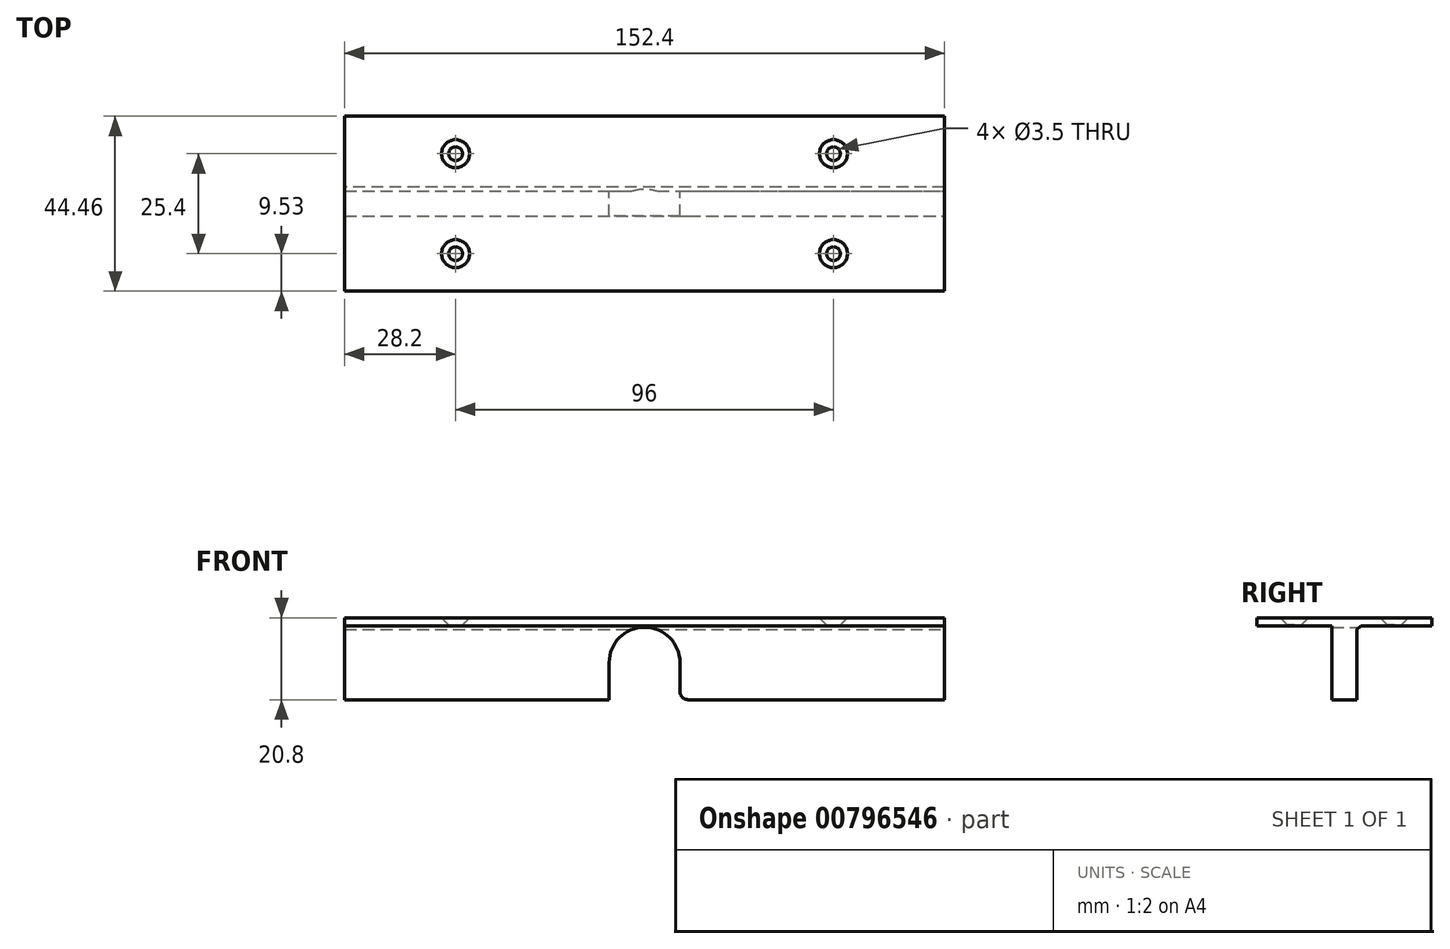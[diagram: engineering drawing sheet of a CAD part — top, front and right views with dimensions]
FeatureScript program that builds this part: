
annotation { "Feature Type Name" : "Feature", "Feature Type Description" : "" }
export const myFeature = defineFeature(function(context is Context, id is Id, definition is map)
    precondition{}
    {
        {
            var Q0;
            Q0=qCreatedBy(makeId("Top.planeOp"),FACE);
            var sketch = newSketch(context, id + "F0", { "sketchPlane" : qUnion([Q0])});
            skLineSegment(sketch, "E0.bottom", {"start": v(76.2, -22.23) * mm, "end": v(-76.2, -22.23) * mm});
            skLineSegment(sketch, "E0.top", {"start": v(76.2, 22.22) * mm, "end": v(-76.2, 22.22) * mm});
            skLineSegment(sketch, "E0.left", {"start": v(76.2, -22.23) * mm, "end": v(76.2, 22.22) * mm});
            skLineSegment(sketch, "E0.right", {"start": v(-76.2, -22.23) * mm, "end": v(-76.2, 22.22) * mm});
            skPoint(sketch, "E0.middle", {"position": v(0, 0) * mm});
            skSolve(sketch);
        }
        {
            var Q0;
            Q0=qSketchRegion(id+"F0",true);
            extrude(context, id + "F1", {"entities" : qUnion([Q0]), "depth" : 2 * mm, "offsetDistance" : 25 * mm});
        }
        {
            var Q0;
            Q0=makeQuery(id+"F1.opExtrude","CAP_FACE",FACE,{"disambiguationData":[OSD([sQuery(id+"F0.wireOp",EDGE,"E0.bottom"),sQuery(id+"F0.wireOp",EDGE,"E0.top"),sQuery(id+"F0.wireOp",EDGE,"E0.left"),sQuery(id+"F0.wireOp",EDGE,"E0.right")])],"isStart":true});
            var sketch = newSketch(context, id + "F2", { "sketchPlane" : qUnion([Q0])});
            skLineSegment(sketch, "E1.bottom", {"start": v(-76.2, -3.18) * mm, "end": v(76.2, -3.18) * mm});
            skLineSegment(sketch, "E1.top", {"start": v(-76.2, 3.17) * mm, "end": v(76.2, 3.17) * mm});
            skLineSegment(sketch, "E1.left", {"start": v(-76.2, -3.18) * mm, "end": v(-76.2, 3.18) * mm});
            skLineSegment(sketch, "E1.right", {"start": v(76.2, -3.18) * mm, "end": v(76.2, 3.18) * mm});
            skPoint(sketch, "E1.middle", {"position": v(0, 0) * mm});
            skSolve(sketch);
        }
        {
            var Q0;
            Q0=makeQuery(id+"F2.imprint","IMPRINT",FACE,{"disambiguationData":[TD([[makeQuery(id+"F2.imprint","IMPRINT",EDGE,{"derivedFrom":sQuery(id+"F2.wireOp",EDGE,"E1.bottom")}),1.0]])]});
            extrude(context, id + "F3", {"entities" : qUnion([Q0]), "operationType" : NewBodyOperationType.ADD, "depth" : 18.8 * mm, "offsetDistance" : 25 * mm});
        }
        {
            var Q0;
            {var subQ0=sQuery(id+"F0.wireOp",EDGE,"E0.right");var subQ1=sQuery(id+"F0.wireOp",EDGE,"E0.left");var subQ2=sQuery(id+"F0.wireOp",EDGE,"E0.top");Q0=makeQuery(id+"F3.boolean.opBoolean","SPLIT",FACE,{"disambiguationData":[TD([makeQuery(id+"F1.opExtrude","SWEPT_FACE",FACE,{"disambiguationData":[OSD([subQ2])]})])],"derivedFrom":makeQuery(id+"F1.opExtrude","CAP_FACE",FACE,{"disambiguationData":[OSD([sQuery(id+"F0.wireOp",EDGE,"E0.bottom"),subQ2,subQ1,subQ0])],"isStart":true})});}
            var sketch = newSketch(context, id + "F4", { "sketchPlane" : qUnion([Q0])});
            skLineSegment(sketch, "E2", {"start": v(76.2, -12.7) * mm, "end": v(-76.2, -12.7) * mm, "construction": true});
            skCircle(sketch, "E3", {"center": v(48, -12.7) * mm, "radius": 1.75 * mm});
            skCircle(sketch, "E4.0.1.0", {"center": v(48, 12.7) * mm, "radius": 1.75 * mm});
            skCircle(sketch, "E4.1.0.0", {"center": v(-48, -12.7) * mm, "radius": 1.75 * mm});
            skCircle(sketch, "E4.1.1.0", {"center": v(-48, 12.7) * mm, "radius": 1.75 * mm});
            skLineSegment(sketch, "E4.direction1", {"start": v(48, -12.7) * mm, "end": v(-48, -12.7) * mm, "construction": true});
            skLineSegment(sketch, "E4.direction2", {"start": v(48, -12.7) * mm, "end": v(48, 12.7) * mm, "construction": true});
            skSolve(sketch);
        }
        {
            var Q0;
            Q0=makeQuery(id+"F4.imprint","IMPRINT",FACE,{"disambiguationData":[TD([[makeQuery(id+"F4.imprint","IMPRINT",EDGE,{"derivedFrom":sQuery(id+"F4.wireOp",EDGE,"E3")}),1.0]])]});
            var Q1;
            Q1=makeQuery(id+"F4.imprint","IMPRINT",FACE,{"disambiguationData":[TD([[makeQuery(id+"F4.imprint","IMPRINT",EDGE,{"derivedFrom":sQuery(id+"F4.wireOp",EDGE,"E4.1.0.0")}),1.0]])]});
            var Q2;
            Q2=makeQuery(id+"F4.imprint","IMPRINT",FACE,{"disambiguationData":[TD([[makeQuery(id+"F4.imprint","IMPRINT",EDGE,{"derivedFrom":sQuery(id+"F4.wireOp",EDGE,"E4.2.0.0")}),1.0]])]});
            var Q3;
            Q3=makeQuery(id+"F4.imprint","IMPRINT",FACE,{"disambiguationData":[TD([[makeQuery(id+"F4.imprint","IMPRINT",EDGE,{"derivedFrom":sQuery(id+"F4.wireOp",EDGE,"E4.3.0.0")}),1.0]])]});
            var Q4;
            Q4=makeQuery(id+"F4.imprint","IMPRINT",FACE,{"disambiguationData":[TD([[makeQuery(id+"F4.imprint","IMPRINT",EDGE,{"derivedFrom":sQuery(id+"F4.wireOp",EDGE,"E4.3.1.0")}),1.0]])]});
            var Q5;
            Q5=makeQuery(id+"F4.imprint","IMPRINT",FACE,{"disambiguationData":[TD([[makeQuery(id+"F4.imprint","IMPRINT",EDGE,{"derivedFrom":sQuery(id+"F4.wireOp",EDGE,"E4.2.1.0")}),1.0]])]});
            var Q6;
            Q6=makeQuery(id+"F4.imprint","IMPRINT",FACE,{"disambiguationData":[TD([[makeQuery(id+"F4.imprint","IMPRINT",EDGE,{"derivedFrom":sQuery(id+"F4.wireOp",EDGE,"E4.1.1.0")}),1.0]])]});
            var Q7;
            Q7=makeQuery(id+"F4.imprint","IMPRINT",FACE,{"disambiguationData":[TD([[makeQuery(id+"F4.imprint","IMPRINT",EDGE,{"derivedFrom":sQuery(id+"F4.wireOp",EDGE,"E4.0.1.0")}),1.0]])]});
            extrude(context, id + "F5", {"entities" : qUnion([Q0, Q1, Q2, Q3, Q4, Q5, Q6, Q7]), "operationType" : NewBodyOperationType.REMOVE, "oppositeDirection" : true, "depth" : 25 * mm, "offsetDistance" : 25 * mm});
        }
        {
            var Q0;
            Q0=makeQuery(id+"F3.opExtrude","SWEPT_FACE",FACE,{"disambiguationData":[OSD([sQuery(id+"F2.wireOp",EDGE,"E1.bottom")])]});
            var sketch = newSketch(context, id + "F6", { "sketchPlane" : qUnion([Q0])});
            skLineSegment(sketch, "E5", {"start": v(-76.2, -9.4) * mm, "end": v(76.2, -9.4) * mm, "construction": true});
            skCircle(sketch, "E6", {"center": v(0, -9.4) * mm, "radius": 9 * mm});
            skCircle(sketch, "E7", {"center": v(0, -9.4) * mm, "radius": 4.76 * mm, "construction": true});
            skPoint(sketch, "E8", {"position": v(9, -9.4) * mm});
            skPoint(sketch, "E9", {"position": v(-9, -9.4) * mm});
            skLineSegment(sketch, "E10", {"start": v(-9, -9.4) * mm, "end": v(-9, -18.8) * mm});
            skLineSegment(sketch, "E11", {"start": v(9, -9.4) * mm, "end": v(9, -18.8) * mm});
            skLineSegment(sketch, "E12", {"start": v(9, -18.8) * mm, "end": v(-9, -18.8) * mm});
            skSolve(sketch);
        }
        {
            var Q0;
            Q0=makeQuery(id+"F6.imprint","IMPRINT",FACE,{"disambiguationData":[TD([[makeQuery(id+"F6.imprint","IMPRINT",EDGE,{"derivedFrom":sQuery(id+"F6.wireOp",EDGE,"E6")}),1.0]])]});
            var Q1;
            {var subQ0=sQuery(id+"F6.wireOp",EDGE,"E10");Q1=makeQuery(id+"F6.imprint","IMPRINT",FACE,{"disambiguationData":[TD([[makeQuery(id+"F6.imprint","IMPRINT",EDGE,{"derivedFrom":subQ0}),1.0]])]});}
            var Q2;
            Q2=sQuery(id+"F6.wireOp",EDGE,"E6");
            extrude(context, id + "F7", {"entities" : qUnion([Q0, Q1]), "operationType" : NewBodyOperationType.REMOVE, "surfaceEntities" : qUnion([Q2]), "endBound" : BoundingType.THROUGH_ALL, "oppositeDirection" : true, "depth" : 25 * mm, "offsetDistance" : 25 * mm});
        }
        {
            var Q0;
            Q0=makeQuery(id+"F5.boolean.opBoolean","INTERSECT",EDGE,{"derivedFrom":[makeQuery(id+"F1.opExtrude","CAP_FACE",FACE,{"disambiguationData":[OSD([sQuery(id+"F0.wireOp",EDGE,"E0.bottom"),sQuery(id+"F0.wireOp",EDGE,"E0.top"),sQuery(id+"F0.wireOp",EDGE,"E0.left"),sQuery(id+"F0.wireOp",EDGE,"E0.right")])],"isStart":false}),makeQuery(id+"F5.opExtrude","SWEPT_FACE",FACE,{"disambiguationData":[OSD([sQuery(id+"F4.wireOp",EDGE,"E4.0.1.0")])]})]});
            var Q1;
            Q1=makeQuery(id+"F5.boolean.opBoolean","INTERSECT",EDGE,{"derivedFrom":[makeQuery(id+"F1.opExtrude","CAP_FACE",FACE,{"disambiguationData":[OSD([sQuery(id+"F0.wireOp",EDGE,"E0.bottom"),sQuery(id+"F0.wireOp",EDGE,"E0.top"),sQuery(id+"F0.wireOp",EDGE,"E0.left"),sQuery(id+"F0.wireOp",EDGE,"E0.right")])],"isStart":false}),makeQuery(id+"F5.opExtrude","SWEPT_FACE",FACE,{"disambiguationData":[OSD([sQuery(id+"F4.wireOp",EDGE,"E4.1.1.0")])]})]});
            var Q2;
            Q2=makeQuery(id+"F5.boolean.opBoolean","INTERSECT",EDGE,{"derivedFrom":[makeQuery(id+"F1.opExtrude","CAP_FACE",FACE,{"disambiguationData":[OSD([sQuery(id+"F0.wireOp",EDGE,"E0.bottom"),sQuery(id+"F0.wireOp",EDGE,"E0.top"),sQuery(id+"F0.wireOp",EDGE,"E0.left"),sQuery(id+"F0.wireOp",EDGE,"E0.right")])],"isStart":false}),makeQuery(id+"F5.opExtrude","SWEPT_FACE",FACE,{"disambiguationData":[OSD([sQuery(id+"F4.wireOp",EDGE,"E4.2.1.0")])]})]});
            var Q3;
            Q3=makeQuery(id+"F5.boolean.opBoolean","INTERSECT",EDGE,{"derivedFrom":[makeQuery(id+"F1.opExtrude","CAP_FACE",FACE,{"disambiguationData":[OSD([sQuery(id+"F0.wireOp",EDGE,"E0.bottom"),sQuery(id+"F0.wireOp",EDGE,"E0.top"),sQuery(id+"F0.wireOp",EDGE,"E0.left"),sQuery(id+"F0.wireOp",EDGE,"E0.right")])],"isStart":false}),makeQuery(id+"F5.opExtrude","SWEPT_FACE",FACE,{"disambiguationData":[OSD([sQuery(id+"F4.wireOp",EDGE,"E4.3.1.0")])]})]});
            var Q4;
            Q4=makeQuery(id+"F5.boolean.opBoolean","INTERSECT",EDGE,{"derivedFrom":[makeQuery(id+"F1.opExtrude","CAP_FACE",FACE,{"disambiguationData":[OSD([sQuery(id+"F0.wireOp",EDGE,"E0.bottom"),sQuery(id+"F0.wireOp",EDGE,"E0.top"),sQuery(id+"F0.wireOp",EDGE,"E0.left"),sQuery(id+"F0.wireOp",EDGE,"E0.right")])],"isStart":false}),makeQuery(id+"F5.opExtrude","SWEPT_FACE",FACE,{"disambiguationData":[OSD([sQuery(id+"F4.wireOp",EDGE,"E4.3.0.0")])]})]});
            var Q5;
            Q5=makeQuery(id+"F5.boolean.opBoolean","INTERSECT",EDGE,{"derivedFrom":[makeQuery(id+"F1.opExtrude","CAP_FACE",FACE,{"disambiguationData":[OSD([sQuery(id+"F0.wireOp",EDGE,"E0.bottom"),sQuery(id+"F0.wireOp",EDGE,"E0.top"),sQuery(id+"F0.wireOp",EDGE,"E0.left"),sQuery(id+"F0.wireOp",EDGE,"E0.right")])],"isStart":false}),makeQuery(id+"F5.opExtrude","SWEPT_FACE",FACE,{"disambiguationData":[OSD([sQuery(id+"F4.wireOp",EDGE,"E4.2.0.0")])]})]});
            var Q6;
            Q6=makeQuery(id+"F5.boolean.opBoolean","INTERSECT",EDGE,{"derivedFrom":[makeQuery(id+"F1.opExtrude","CAP_FACE",FACE,{"disambiguationData":[OSD([sQuery(id+"F0.wireOp",EDGE,"E0.bottom"),sQuery(id+"F0.wireOp",EDGE,"E0.top"),sQuery(id+"F0.wireOp",EDGE,"E0.left"),sQuery(id+"F0.wireOp",EDGE,"E0.right")])],"isStart":false}),makeQuery(id+"F5.opExtrude","SWEPT_FACE",FACE,{"disambiguationData":[OSD([sQuery(id+"F4.wireOp",EDGE,"E4.1.0.0")])]})]});
            var Q7;
            Q7=makeQuery(id+"F5.boolean.opBoolean","INTERSECT",EDGE,{"derivedFrom":[makeQuery(id+"F1.opExtrude","CAP_FACE",FACE,{"disambiguationData":[OSD([sQuery(id+"F0.wireOp",EDGE,"E0.bottom"),sQuery(id+"F0.wireOp",EDGE,"E0.top"),sQuery(id+"F0.wireOp",EDGE,"E0.left"),sQuery(id+"F0.wireOp",EDGE,"E0.right")])],"isStart":false}),makeQuery(id+"F5.opExtrude","SWEPT_FACE",FACE,{"disambiguationData":[OSD([sQuery(id+"F4.wireOp",EDGE,"E3")])]})]});
            chamfer(context, id + "F8", {"entities" : qUnion([Q0, Q1, Q2, Q3, Q4, Q5, Q6, Q7]), "width" : 1.8 * mm, "tangentPropagation" : true});
        }
        {
            var Q0;
            Q0=makeQuery(id+"F3.opExtrude","CAP_EDGE",EDGE,{"disambiguationData":[OSD([sQuery(id+"F2.wireOp",EDGE,"E1.bottom")])],"isStart":true});
            var Q1;
            Q1=makeQuery(id+"F3.opExtrude","CAP_EDGE",EDGE,{"disambiguationData":[OSD([sQuery(id+"F2.wireOp",EDGE,"E1.top")])],"isStart":true});
            chamfer(context, id + "F9", {"entities" : qUnion([Q0, Q1]), "width" : 1 * mm, "tangentPropagation" : true});
        }
        {
            var Q0;
            Q0=makeQuery(id+"F7.boolean.opBoolean","COPY",EDGE,{"derivedFrom":makeQuery(id+"F7.opExtrude","SWEPT_EDGE",EDGE,{"disambiguationData":[OSD([sQuery(id+"F2.wireOp",EDGE,"E1.bottom"),sQuery(id+"F6.wireOp",EDGE,"E10"),sQuery(id+"F6.wireOp",EDGE,"E12")])]})});
            var Q1;
            Q1=makeQuery(id+"F7.boolean.opBoolean","COPY",EDGE,{"derivedFrom":makeQuery(id+"F7.opExtrude","SWEPT_EDGE",EDGE,{"disambiguationData":[OSD([sQuery(id+"F2.wireOp",EDGE,"E1.bottom"),sQuery(id+"F6.wireOp",EDGE,"E11"),sQuery(id+"F6.wireOp",EDGE,"E12")])]})});
            fillet(context, id + "F10", {"entities" : qUnion([Q0, Q1]), "radius" : 2 * mm, "tangentPropagation" : true, "allowEdgeOverflow" : false});
        }
    });
